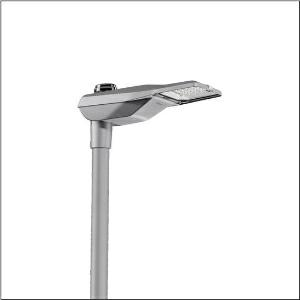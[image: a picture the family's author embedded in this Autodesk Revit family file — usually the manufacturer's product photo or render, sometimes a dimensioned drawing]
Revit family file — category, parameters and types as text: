
# Revit family: streetlight_sl_21_micro___st1_5a_5xe5p37n08cb_e60d
name_source: partatom
category: Lighting Fixtures
units: mm (PartAtom-declared; Revit-internal decimal feet)

## family parameters
Cut with Voids When Loaded = No
Host = Face
Light Source = No
Part Type = Normal
Room Calculation Point = No
Round Connector Dimension = Use Diameter
Shared = No

## types (1)
- --- (1 x LED, 2250 lm, 15.8 W, 3000K)
    Apparent Load = 16 VA
    CIE Flux Codes = 22 53 95 100 100
    Color Rendering = 70
    Color Temperature = 3000K
    Default Elevation = 1800 mm
    Description = Streetlight SL 21 micro, mast luminaire, primary light control with lens, of PMMA, primary optical cover: cover, of toughened safety glass, transparent, light distribution: ST1.5a, light emission: direct distribution, primary light characteristic: asymmetric, installation type: post-top, LED, 3G 1.5mm², High Power LED, rated luminous flux: 2.250lm, luminous efficacy: 142lm/W, light colour: 730, colour temperature: 3000K, control: overheat protection, pre-setting: linear dimming characteristic, constant luminous flux control, time-dependent luminous flux control, flexible luminous flux parameterisation, mains connection: 230..240V, AC, 50/60Hz, connection cable pre-assembled, cable length: 6,5m, wiring characteristics: H07RN-F, start of lifetime: 16W, end of service life: 16W, reduction: 8W, luminaire housing, of diecast aluminium (EN AC-44300), powder-coated, Siteco® metallic grey (DB 702S), corrosivity category C5 mid according to DIN EN ISO 12944, multi-level sealing system, sealing non-destructively replaceable, inclination adjustable: 0°, 5°, 10°, 15°, length: 528mm, width: 235mm, height: 110mm, spigot size: 76/60mm (post-top), protection rating (complete): IP66, insulation class (complete): insulation class I (protective earthing), certification: CE, ENEC, ENEC+, VDE, impact resistance: IK09, permissible operating ambient temperature for outdoor applications: -40..+50°C, standard-compliant lighting for roads and squares, packaging unit: 1 piece

Light Distribution: ST1.5a
    Height = 110 mm
    Lamp = 1 x LED
    Lamp Light Flux = 2250 lm
    Lamp Power = 15.8 W
    Lamp count = 1
    Length = 528 mm
    Luminous efficacy = 142 lm/W
    Manufacturer = Siteco
    ModVariant = No
    Model = 5XE5P37N08CB
    Number of Poles = 1
    OnlyDefault = Yes
    Power Factor = 1
    Product Name = Streetlight SL 21 micro | ST1.5a
    Product group = mast luminaire | pylon top
    ProductGroupID = 6100
    Protection Class = Protection class I
    Protection Degree = IP 66
    RLX_Detail_Level = 1
    RLX_Emergency_Light_Flux = 0 lm
    RLX_Emergency_Type = 0
    RLX_Emergency_Type_DB = No
    RlxData = <blob elided: 102725 chars, md5=0f2298f2>
    Socket = socket
    Standby Power = 0 W
    System Light Flux = 2250 lm
    System Power = 16 W
    Type Comments = factory setting: luminous flux: 100 % | dim-lin: 254 | 300 mA
    Type Image = l_1294375.jpg
    URL = http://relux.com
    VarID = @adj_103607
    Voltage = 0 V
    Weight = 0.00 kg
    Width = 235 mm

## geometry (parser evidence)
native form markers: Blend x4, Sweep x9
no freeform markers — native parametric forms only
